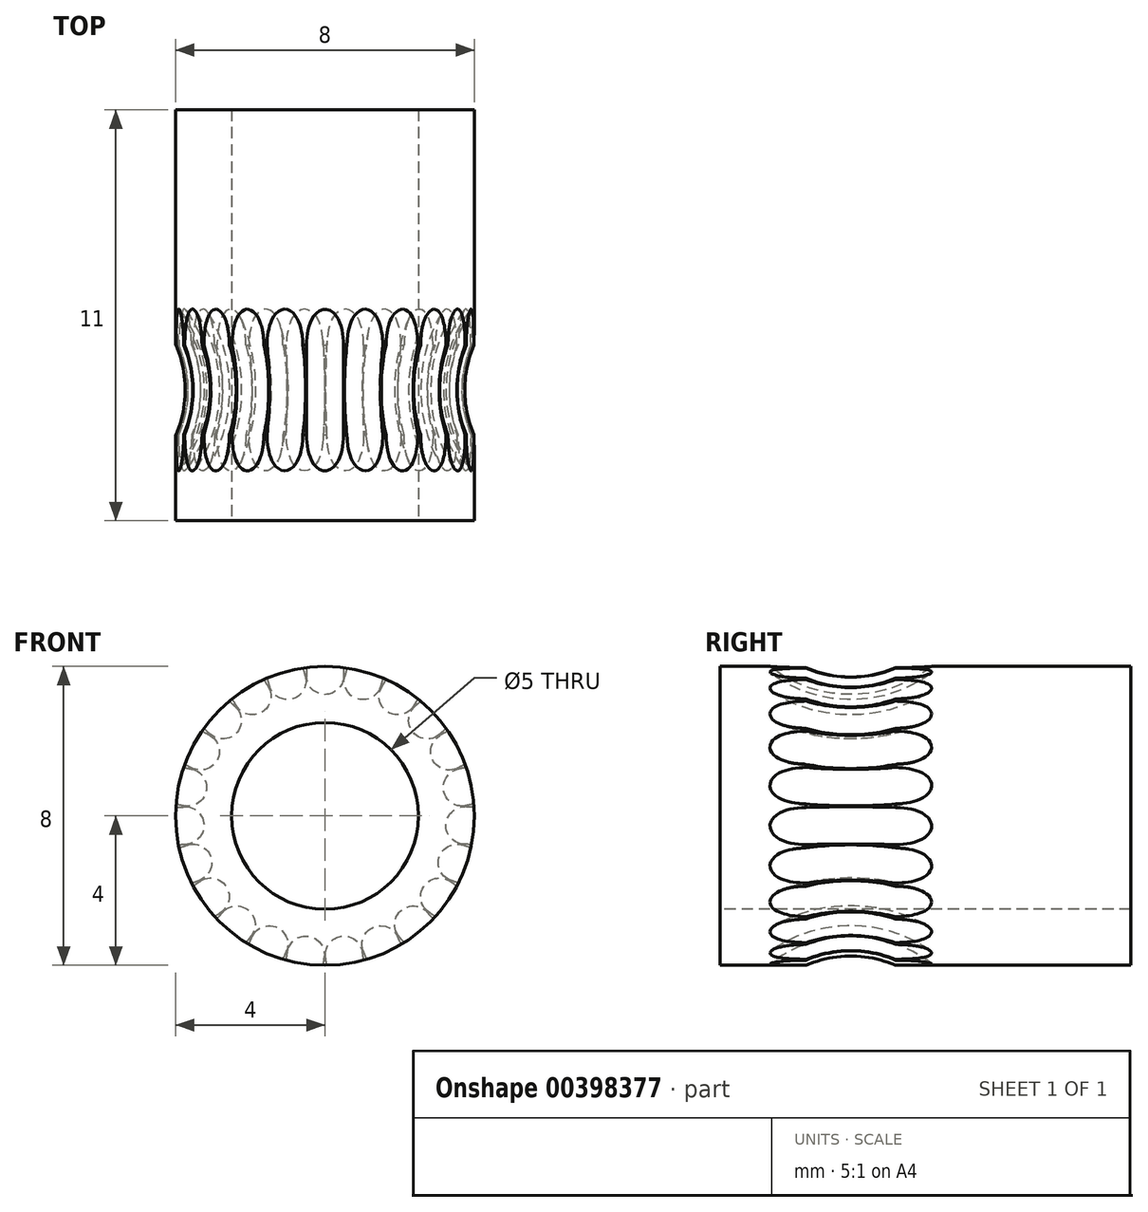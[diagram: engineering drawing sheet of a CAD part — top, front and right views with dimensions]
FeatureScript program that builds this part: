
annotation { "Feature Type Name" : "Feature", "Feature Type Description" : "" }
export const myFeature = defineFeature(function(context is Context, id is Id, definition is map)
    precondition{}
    {
        {
            var Q0;
            Q0=qCreatedBy(makeId("Right.planeOp"),FACE);
            var sketch = newSketch(context, id + "F0", { "sketchPlane" : qUnion([Q0])});
            skLineSegment(sketch, "E0", {"start": v(0, 4) * mm, "end": v(0, 2.5) * mm});
            skLineSegment(sketch, "E1", {"start": v(0, 2.5) * mm, "end": v(11, 2.5) * mm});
            skLineSegment(sketch, "E2", {"start": v(11, 2.5) * mm, "end": v(11, 4) * mm});
            skLineSegment(sketch, "E3", {"start": v(11, 4) * mm, "end": v(4.7, 4) * mm});
            skLineSegment(sketch, "E4", {"start": v(0, 4) * mm, "end": v(2.3, 4) * mm});
            skArc(sketch, "E5", {"start": v(2.3, 4) * mm, "mid": v(3.5, 3.75) * mm, "end": v(4.7, 4) * mm});
            skSolve(sketch);
        }
        {
            var Q0;
            Q0=qCreatedBy(makeId("Right.planeOp"),FACE);
            var sketch = newSketch(context, id + "F1", { "sketchPlane" : qUnion([Q0])});
            skLineSegment(sketch, "E6", {"start": v(0, 0) * mm, "end": v(11, 0) * mm});
            skSolve(sketch);
        }
        {
            var Q0;
            Q0 = qSketchRegion(id + "F0", true);
            var Q1;
            Q1=sQuery(id+"F1.wireOp",EDGE,"E6");
            revolve(context, id + "F2", {"entities" : qUnion([Q0]), "axis" : qUnion([Q1]), "revolveType" : RevolveType.FULL});
        }
        {
            var Q0;
            Q0=qCreatedBy(makeId("Right.planeOp"),FACE);
            var sketch = newSketch(context, id + "F3", { "sketchPlane" : qUnion([Q0])});
            skLineSegment(sketch, "E7", {"start": v(0, 6.75) * mm, "end": v(0, 8.75) * mm});
            skLineSegment(sketch, "E8", {"start": v(0, 8.75) * mm, "end": v(7, 8.75) * mm});
            skLineSegment(sketch, "E9", {"start": v(7, 8.75) * mm, "end": v(7, 6.75) * mm});
            skArc(sketch, "E10", {"start": v(0, 6.75) * mm, "mid": v(3.5, 3.25) * mm, "end": v(7, 6.75) * mm});
            skSolve(sketch);
        }
        {
            var Q0;
            Q0=makeQuery(id+"F3.imprint","IMPRINT",FACE,{"disambiguationData":[TD([[makeQuery(id+"F3.imprint","IMPRINT",EDGE,{"derivedFrom":sQuery(id+"F3.wireOp",EDGE,"E7")}),-1.0]])]});
            extrude(context, id + "F4", {"entities" : qUnion([Q0]), "endBound" : BoundingType.SYMMETRIC, "depth" : 1 * mm, "hasSecondDirection" : true, "secondDirectionOppositeDirection" : true, "secondDirectionDepth" : 25 * mm});
        }
        {
            var Q0;
            Q0=makeQuery(id+"F4.opExtrude","CAP_EDGE",EDGE,{"disambiguationData":[OSD([sQuery(id+"F3.wireOp",EDGE,"E10")])],"isStart":false});
            var Q1;
            Q1=makeQuery(id+"F4.opExtrude","CAP_EDGE",EDGE,{"disambiguationData":[OSD([sQuery(id+"F3.wireOp",EDGE,"E10")])],"isStart":true});
            fillet(context, id + "F5", {"entities" : qUnion([Q0, Q1]), "radius" : 0.5 * mm, "tangentPropagation" : true, "allowEdgeOverflow" : false});
        }
        {
            var Q0;
            Q0=makeQuery(id+"F4.opExtrude","SWEPT_BODY",BODY,{"disambiguationData":[OSD([sQuery(id+"F3.wireOp",EDGE,"E7"),sQuery(id+"F3.wireOp",EDGE,"E8"),sQuery(id+"F3.wireOp",EDGE,"E9"),sQuery(id+"F3.wireOp",EDGE,"E10")])]});
            var Q1;
            Q1=sQuery(id+"F1.wireOp",EDGE,"E6");
            circularPattern(context, id + "F6", {"entities" : qUnion([Q0]), "axis" : qUnion([Q1]), "angle" : 360 * degree, "instanceCount" : 23, "equalSpace" : true});
        }
        {
            var Q0;
            Q0=makeQuery(id+"F4.opExtrude","SWEPT_BODY",BODY,{"disambiguationData":[OSD([sQuery(id+"F3.wireOp",EDGE,"E7"),sQuery(id+"F3.wireOp",EDGE,"E8"),sQuery(id+"F3.wireOp",EDGE,"E9"),sQuery(id+"F3.wireOp",EDGE,"E10")])]});
            var Q1;
            Q1=makeQuery(id+"F6.opPattern","COPY",BODY,{"derivedFrom":makeQuery(id+"F4.opExtrude","SWEPT_BODY",BODY,{"disambiguationData":[OSD([sQuery(id+"F3.wireOp",EDGE,"E7"),sQuery(id+"F3.wireOp",EDGE,"E8"),sQuery(id+"F3.wireOp",EDGE,"E9"),sQuery(id+"F3.wireOp",EDGE,"E10")])]}),"instanceName":"1"});
            var Q2;
            Q2=makeQuery(id+"F6.opPattern","COPY",BODY,{"derivedFrom":makeQuery(id+"F4.opExtrude","SWEPT_BODY",BODY,{"disambiguationData":[OSD([sQuery(id+"F3.wireOp",EDGE,"E7"),sQuery(id+"F3.wireOp",EDGE,"E8"),sQuery(id+"F3.wireOp",EDGE,"E9"),sQuery(id+"F3.wireOp",EDGE,"E10")])]}),"instanceName":"2"});
            var Q3;
            Q3=makeQuery(id+"F6.opPattern","COPY",BODY,{"derivedFrom":makeQuery(id+"F4.opExtrude","SWEPT_BODY",BODY,{"disambiguationData":[OSD([sQuery(id+"F3.wireOp",EDGE,"E7"),sQuery(id+"F3.wireOp",EDGE,"E8"),sQuery(id+"F3.wireOp",EDGE,"E9"),sQuery(id+"F3.wireOp",EDGE,"E10")])]}),"instanceName":"3"});
            var Q4;
            Q4=makeQuery(id+"F6.opPattern","COPY",BODY,{"derivedFrom":makeQuery(id+"F4.opExtrude","SWEPT_BODY",BODY,{"disambiguationData":[OSD([sQuery(id+"F3.wireOp",EDGE,"E7"),sQuery(id+"F3.wireOp",EDGE,"E8"),sQuery(id+"F3.wireOp",EDGE,"E9"),sQuery(id+"F3.wireOp",EDGE,"E10")])]}),"instanceName":"4"});
            var Q5;
            Q5=makeQuery(id+"F6.opPattern","COPY",BODY,{"derivedFrom":makeQuery(id+"F4.opExtrude","SWEPT_BODY",BODY,{"disambiguationData":[OSD([sQuery(id+"F3.wireOp",EDGE,"E7"),sQuery(id+"F3.wireOp",EDGE,"E8"),sQuery(id+"F3.wireOp",EDGE,"E9"),sQuery(id+"F3.wireOp",EDGE,"E10")])]}),"instanceName":"5"});
            var Q6;
            Q6=makeQuery(id+"F6.opPattern","COPY",BODY,{"derivedFrom":makeQuery(id+"F4.opExtrude","SWEPT_BODY",BODY,{"disambiguationData":[OSD([sQuery(id+"F3.wireOp",EDGE,"E7"),sQuery(id+"F3.wireOp",EDGE,"E8"),sQuery(id+"F3.wireOp",EDGE,"E9"),sQuery(id+"F3.wireOp",EDGE,"E10")])]}),"instanceName":"6"});
            var Q7;
            Q7=makeQuery(id+"F6.opPattern","COPY",BODY,{"derivedFrom":makeQuery(id+"F4.opExtrude","SWEPT_BODY",BODY,{"disambiguationData":[OSD([sQuery(id+"F3.wireOp",EDGE,"E7"),sQuery(id+"F3.wireOp",EDGE,"E8"),sQuery(id+"F3.wireOp",EDGE,"E9"),sQuery(id+"F3.wireOp",EDGE,"E10")])]}),"instanceName":"22"});
            var Q8;
            Q8=makeQuery(id+"F6.opPattern","COPY",BODY,{"derivedFrom":makeQuery(id+"F4.opExtrude","SWEPT_BODY",BODY,{"disambiguationData":[OSD([sQuery(id+"F3.wireOp",EDGE,"E7"),sQuery(id+"F3.wireOp",EDGE,"E8"),sQuery(id+"F3.wireOp",EDGE,"E9"),sQuery(id+"F3.wireOp",EDGE,"E10")])]}),"instanceName":"21"});
            var Q9;
            Q9=makeQuery(id+"F6.opPattern","COPY",BODY,{"derivedFrom":makeQuery(id+"F4.opExtrude","SWEPT_BODY",BODY,{"disambiguationData":[OSD([sQuery(id+"F3.wireOp",EDGE,"E7"),sQuery(id+"F3.wireOp",EDGE,"E8"),sQuery(id+"F3.wireOp",EDGE,"E9"),sQuery(id+"F3.wireOp",EDGE,"E10")])]}),"instanceName":"20"});
            var Q10;
            Q10=makeQuery(id+"F6.opPattern","COPY",BODY,{"derivedFrom":makeQuery(id+"F4.opExtrude","SWEPT_BODY",BODY,{"disambiguationData":[OSD([sQuery(id+"F3.wireOp",EDGE,"E7"),sQuery(id+"F3.wireOp",EDGE,"E8"),sQuery(id+"F3.wireOp",EDGE,"E9"),sQuery(id+"F3.wireOp",EDGE,"E10")])]}),"instanceName":"19"});
            var Q11;
            Q11=makeQuery(id+"F6.opPattern","COPY",BODY,{"derivedFrom":makeQuery(id+"F4.opExtrude","SWEPT_BODY",BODY,{"disambiguationData":[OSD([sQuery(id+"F3.wireOp",EDGE,"E7"),sQuery(id+"F3.wireOp",EDGE,"E8"),sQuery(id+"F3.wireOp",EDGE,"E9"),sQuery(id+"F3.wireOp",EDGE,"E10")])]}),"instanceName":"16"});
            var Q12;
            Q12=makeQuery(id+"F6.opPattern","COPY",BODY,{"derivedFrom":makeQuery(id+"F4.opExtrude","SWEPT_BODY",BODY,{"disambiguationData":[OSD([sQuery(id+"F3.wireOp",EDGE,"E7"),sQuery(id+"F3.wireOp",EDGE,"E8"),sQuery(id+"F3.wireOp",EDGE,"E9"),sQuery(id+"F3.wireOp",EDGE,"E10")])]}),"instanceName":"18"});
            var Q13;
            Q13=makeQuery(id+"F6.opPattern","COPY",BODY,{"derivedFrom":makeQuery(id+"F4.opExtrude","SWEPT_BODY",BODY,{"disambiguationData":[OSD([sQuery(id+"F3.wireOp",EDGE,"E7"),sQuery(id+"F3.wireOp",EDGE,"E8"),sQuery(id+"F3.wireOp",EDGE,"E9"),sQuery(id+"F3.wireOp",EDGE,"E10")])]}),"instanceName":"17"});
            var Q14;
            Q14=makeQuery(id+"F6.opPattern","COPY",BODY,{"derivedFrom":makeQuery(id+"F4.opExtrude","SWEPT_BODY",BODY,{"disambiguationData":[OSD([sQuery(id+"F3.wireOp",EDGE,"E7"),sQuery(id+"F3.wireOp",EDGE,"E8"),sQuery(id+"F3.wireOp",EDGE,"E9"),sQuery(id+"F3.wireOp",EDGE,"E10")])]}),"instanceName":"15"});
            var Q15;
            Q15=makeQuery(id+"F6.opPattern","COPY",BODY,{"derivedFrom":makeQuery(id+"F4.opExtrude","SWEPT_BODY",BODY,{"disambiguationData":[OSD([sQuery(id+"F3.wireOp",EDGE,"E7"),sQuery(id+"F3.wireOp",EDGE,"E8"),sQuery(id+"F3.wireOp",EDGE,"E9"),sQuery(id+"F3.wireOp",EDGE,"E10")])]}),"instanceName":"14"});
            var Q16;
            Q16=makeQuery(id+"F6.opPattern","COPY",BODY,{"derivedFrom":makeQuery(id+"F4.opExtrude","SWEPT_BODY",BODY,{"disambiguationData":[OSD([sQuery(id+"F3.wireOp",EDGE,"E7"),sQuery(id+"F3.wireOp",EDGE,"E8"),sQuery(id+"F3.wireOp",EDGE,"E9"),sQuery(id+"F3.wireOp",EDGE,"E10")])]}),"instanceName":"13"});
            var Q17;
            Q17=makeQuery(id+"F6.opPattern","COPY",BODY,{"derivedFrom":makeQuery(id+"F4.opExtrude","SWEPT_BODY",BODY,{"disambiguationData":[OSD([sQuery(id+"F3.wireOp",EDGE,"E7"),sQuery(id+"F3.wireOp",EDGE,"E8"),sQuery(id+"F3.wireOp",EDGE,"E9"),sQuery(id+"F3.wireOp",EDGE,"E10")])]}),"instanceName":"23"});
            var Q18;
            Q18=makeQuery(id+"F6.opPattern","COPY",BODY,{"derivedFrom":makeQuery(id+"F4.opExtrude","SWEPT_BODY",BODY,{"disambiguationData":[OSD([sQuery(id+"F3.wireOp",EDGE,"E7"),sQuery(id+"F3.wireOp",EDGE,"E8"),sQuery(id+"F3.wireOp",EDGE,"E9"),sQuery(id+"F3.wireOp",EDGE,"E10")])]}),"instanceName":"7"});
            var Q19;
            Q19=makeQuery(id+"F6.opPattern","COPY",BODY,{"derivedFrom":makeQuery(id+"F4.opExtrude","SWEPT_BODY",BODY,{"disambiguationData":[OSD([sQuery(id+"F3.wireOp",EDGE,"E7"),sQuery(id+"F3.wireOp",EDGE,"E8"),sQuery(id+"F3.wireOp",EDGE,"E9"),sQuery(id+"F3.wireOp",EDGE,"E10")])]}),"instanceName":"8"});
            var Q20;
            Q20=makeQuery(id+"F6.opPattern","COPY",BODY,{"derivedFrom":makeQuery(id+"F4.opExtrude","SWEPT_BODY",BODY,{"disambiguationData":[OSD([sQuery(id+"F3.wireOp",EDGE,"E7"),sQuery(id+"F3.wireOp",EDGE,"E8"),sQuery(id+"F3.wireOp",EDGE,"E9"),sQuery(id+"F3.wireOp",EDGE,"E10")])]}),"instanceName":"9"});
            var Q21;
            Q21=makeQuery(id+"F6.opPattern","COPY",BODY,{"derivedFrom":makeQuery(id+"F4.opExtrude","SWEPT_BODY",BODY,{"disambiguationData":[OSD([sQuery(id+"F3.wireOp",EDGE,"E7"),sQuery(id+"F3.wireOp",EDGE,"E8"),sQuery(id+"F3.wireOp",EDGE,"E9"),sQuery(id+"F3.wireOp",EDGE,"E10")])]}),"instanceName":"10"});
            var Q22;
            Q22=makeQuery(id+"F6.opPattern","COPY",BODY,{"derivedFrom":makeQuery(id+"F4.opExtrude","SWEPT_BODY",BODY,{"disambiguationData":[OSD([sQuery(id+"F3.wireOp",EDGE,"E7"),sQuery(id+"F3.wireOp",EDGE,"E8"),sQuery(id+"F3.wireOp",EDGE,"E9"),sQuery(id+"F3.wireOp",EDGE,"E10")])]}),"instanceName":"11"});
            var Q23;
            Q23=makeQuery(id+"F6.opPattern","COPY",BODY,{"derivedFrom":makeQuery(id+"F4.opExtrude","SWEPT_BODY",BODY,{"disambiguationData":[OSD([sQuery(id+"F3.wireOp",EDGE,"E7"),sQuery(id+"F3.wireOp",EDGE,"E8"),sQuery(id+"F3.wireOp",EDGE,"E9"),sQuery(id+"F3.wireOp",EDGE,"E10")])]}),"instanceName":"12"});
            var Q24;
            Q24=makeQuery(id+"F2.opRevolve","SWEPT_BODY",BODY,{"disambiguationData":[OSD([sQuery(id+"F0.wireOp",EDGE,"E0"),sQuery(id+"F0.wireOp",EDGE,"E1"),sQuery(id+"F0.wireOp",EDGE,"E2"),sQuery(id+"F0.wireOp",EDGE,"E3"),sQuery(id+"F0.wireOp",EDGE,"E4"),sQuery(id+"F0.wireOp",EDGE,"E5")])]});
            booleanBodies(context, id + "F7", {"operationType" : BooleanOperationType.SUBTRACTION, "tools" : qUnion([Q0, Q1, Q2, Q3, Q4, Q5, Q6, Q7, Q8, Q9, Q10, Q11, Q12, Q13, Q14, Q15, Q16, Q17, Q18, Q19, Q20, Q21, Q22, Q23]), "targets" : qUnion([Q24])});
        }
    });
